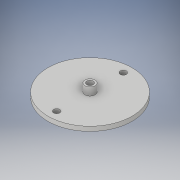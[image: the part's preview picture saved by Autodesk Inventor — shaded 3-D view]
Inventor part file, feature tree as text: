
AUTODESK INVENTOR PART (.ipt)
format: ipt  version: 2018 (Build 220112000, 112)  size: 126,464 bytes
history: native  units: in
note: dims shown in document units (in); Inventor stores cm internally (conversion verified against a paired STEP export)
features: sketch x6, extrude x4, hole x2
ambient origin geometry x8: Origin, YZ Plane, XZ Plane, XY Plane, X Axis, Y Axis, Z Axis, Center Point
bodies: Solid1 (feature_tree)
feature tree (12):
  extrude  "Extrusion1"  Depth=0.08in TaperAngle=0.0deg
  extrude  "Extrusion3"  Depth=0.14in TaperAngle=0.0deg
  extrude  "Extrusion4"  Depth=0.18in TaperAngle=0.0deg
  extrude  "Extrusion5"  Depth=0.18in TaperAngle=0.0deg
  hole  "Hole2"  [1 undecoded]
  hole  "Hole3"  [1 undecoded]
  sketch  "Sketch1"  dims[d0=1.5in d1=0.08in d2=0.0in]
  sketch  "Sketch5"  dims[d14=0.18in d15=0.14in d16=0.0in]
  sketch  "Sketch6"  dims[d17=0.115in d18=0.18in d19=0.0in]
  sketch  "Sketch7"  dims[d20=0.08in d21=0.18in d22=0.0in]
  sketch  "Sketch8"  dims[d23=0.155in d24=0.155in]
  sketch  "Sketch9"  dims[d25=0.11in d26=0.75in d27=0.375in d28=0.25in d29=0.5635in d30=0.2in d31=0.8108in d32=0.155in d33=0.11in d34=0.75in d35=0.375in d36=0.25in d37=0.5635in d38=0.2in d39=0.8108in]
note: 2 required parameter values undecoded (feature->parameter linkage not recoverable at this tier; creation-order binding heuristic only, values carry confidence <= 0.55)
